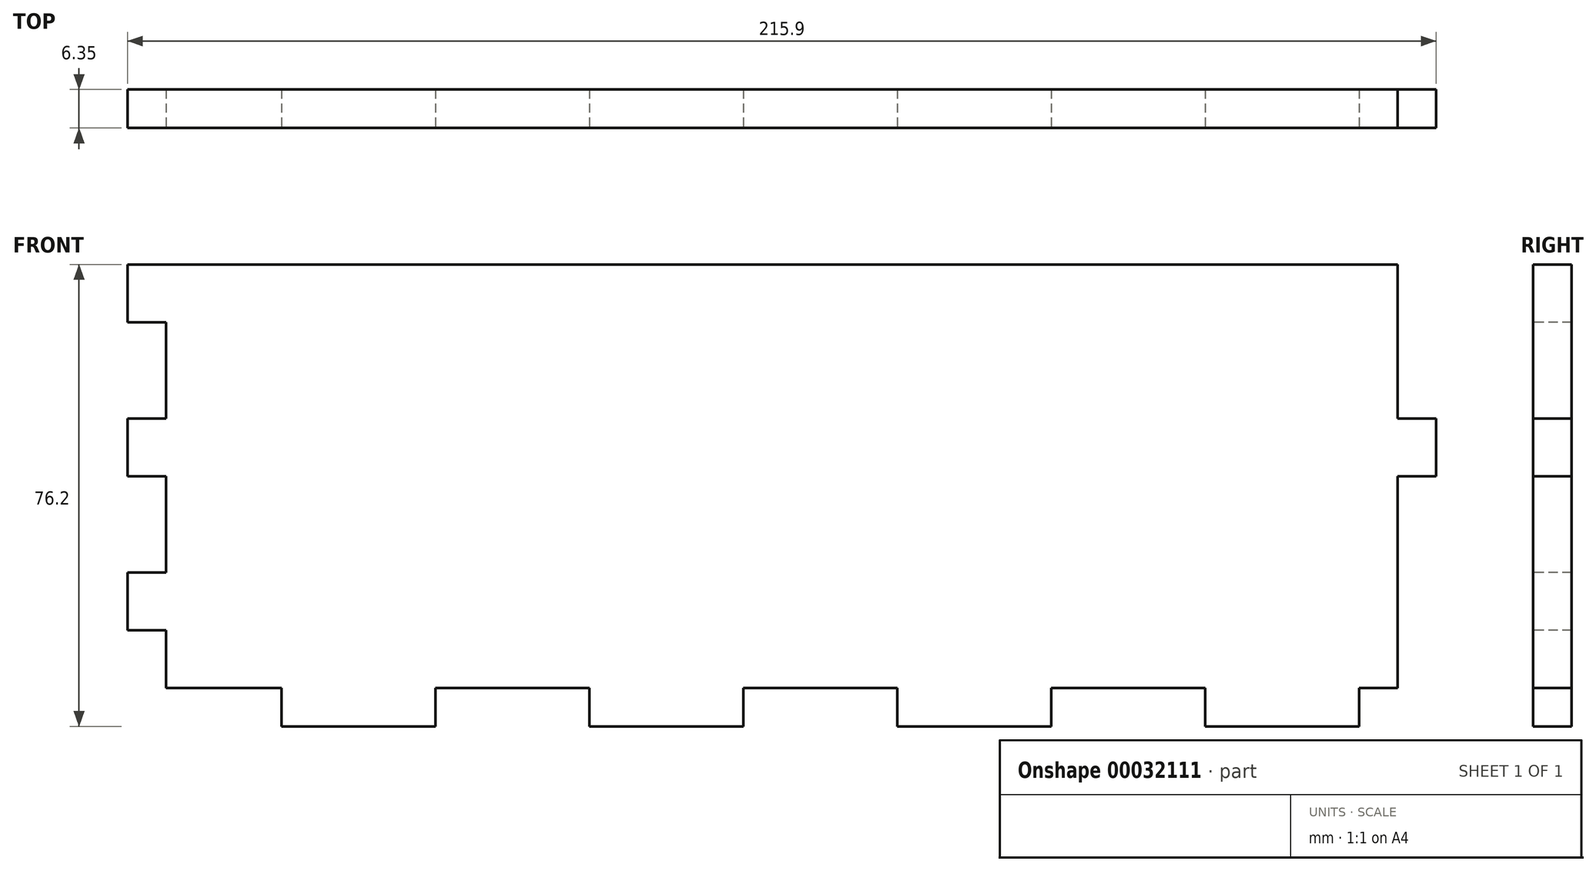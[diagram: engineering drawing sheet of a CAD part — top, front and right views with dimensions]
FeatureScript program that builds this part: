
annotation { "Feature Type Name" : "Feature", "Feature Type Description" : "" }
export const myFeature = defineFeature(function(context is Context, id is Id, definition is map)
    precondition{}
    {
        {
            var Q0;
            Q0=qCreatedBy(makeId("Front.planeOp"),FACE);
            var sketch = newSketch(context, id + "F0", { "sketchPlane" : qUnion([Q0])});
            skLineSegment(sketch, "E0.bottom", {"start": v(0, 0) * mm, "end": v(215.9, 0) * mm});
            skLineSegment(sketch, "E0.top", {"start": v(0, 76.2) * mm, "end": v(215.9, 76.2) * mm});
            skLineSegment(sketch, "E0.left", {"start": v(0, 0) * mm, "end": v(0, 76.2) * mm});
            skLineSegment(sketch, "E0.right", {"start": v(215.9, 0) * mm, "end": v(215.9, 76.2) * mm});
            skSolve(sketch);
        }
        {
            var Q0;
            Q0=makeQuery(id+"F0.imprint","IMPRINT",FACE,{"disambiguationData":[TD([[makeQuery(id+"F0.imprint","IMPRINT",EDGE,{"derivedFrom":sQuery(id+"F0.wireOp",EDGE,"E0.bottom")}),1.0]])]});
            extrude(context, id + "F1", {"entities" : qUnion([Q0]), "depth" : 6.35 * mm});
        }
        {
            var Q0;
            Q0=makeQuery(id+"F1.opExtrude","CAP_FACE",FACE,{"disambiguationData":[OSD([sQuery(id+"F0.wireOp",EDGE,"E0.bottom"),sQuery(id+"F0.wireOp",EDGE,"E0.top"),sQuery(id+"F0.wireOp",EDGE,"E0.left"),sQuery(id+"F0.wireOp",EDGE,"E0.right")])],"isStart":false});
            var sketch = newSketch(context, id + "F2", { "sketchPlane" : qUnion([Q0])});
            skLineSegment(sketch, "E1.bottom", {"start": v(0, 66.68) * mm, "end": v(6.35, 66.68) * mm});
            skLineSegment(sketch, "E1.top", {"start": v(0, 50.8) * mm, "end": v(6.35, 50.8) * mm});
            skLineSegment(sketch, "E1.left", {"start": v(0, 66.68) * mm, "end": v(0, 50.8) * mm});
            skLineSegment(sketch, "E1.right", {"start": v(6.35, 66.68) * mm, "end": v(6.35, 50.8) * mm});
            skLineSegment(sketch, "E2.bottom", {"start": v(0, 41.28) * mm, "end": v(6.35, 41.28) * mm});
            skLineSegment(sketch, "E2.top", {"start": v(0, 25.4) * mm, "end": v(6.35, 25.4) * mm});
            skLineSegment(sketch, "E2.left", {"start": v(0, 41.28) * mm, "end": v(0, 25.4) * mm});
            skLineSegment(sketch, "E2.right", {"start": v(6.35, 41.28) * mm, "end": v(6.35, 25.4) * mm});
            skLineSegment(sketch, "E3.bottom", {"start": v(0, 15.88) * mm, "end": v(6.35, 15.88) * mm});
            skLineSegment(sketch, "E3.top", {"start": v(0, 6.35) * mm, "end": v(6.35, 6.35) * mm});
            skLineSegment(sketch, "E3.left", {"start": v(0, 15.88) * mm, "end": v(0, 6.35) * mm});
            skLineSegment(sketch, "E3.right", {"start": v(6.35, 15.88) * mm, "end": v(6.35, 6.35) * mm});
            skLineSegment(sketch, "E4", {"start": v(107.95, 76.2) * mm, "end": v(107.95, 0) * mm, "construction": true});
            skLineSegment(sketch, "E5.MirrorCS", {"start": v(209.55, 15.88) * mm, "end": v(209.55, 6.35) * mm});
            skLineSegment(sketch, "E6.MirrorCS", {"start": v(215.9, 15.88) * mm, "end": v(215.9, 6.35) * mm});
            skLineSegment(sketch, "E7.MirrorCS", {"start": v(215.9, 6.35) * mm, "end": v(209.55, 6.35) * mm});
            skLineSegment(sketch, "E8.MirrorCS", {"start": v(215.9, 15.88) * mm, "end": v(209.55, 15.88) * mm});
            skLineSegment(sketch, "E9.MirrorCS", {"start": v(215.9, 41.28) * mm, "end": v(209.55, 41.28) * mm});
            skLineSegment(sketch, "E10.MirrorCS", {"start": v(215.9, 25.4) * mm, "end": v(209.55, 25.4) * mm});
            skLineSegment(sketch, "E11.MirrorCS", {"start": v(215.9, 66.68) * mm, "end": v(209.55, 66.68) * mm});
            skLineSegment(sketch, "E12.MirrorCS", {"start": v(215.9, 50.8) * mm, "end": v(209.55, 50.8) * mm});
            skLineSegment(sketch, "E13.MirrorCS", {"start": v(209.55, 41.28) * mm, "end": v(209.55, 25.4) * mm});
            skLineSegment(sketch, "E14.MirrorCS", {"start": v(215.9, 41.28) * mm, "end": v(215.9, 25.4) * mm});
            skLineSegment(sketch, "E15.MirrorCS", {"start": v(209.55, 66.68) * mm, "end": v(209.55, 50.8) * mm});
            skLineSegment(sketch, "E16.MirrorCS", {"start": v(215.9, 66.68) * mm, "end": v(215.9, 50.8) * mm});
            skSolve(sketch);
        }
        {
            var Q0;
            Q0 = qSketchRegion(id + "F2", true);
            extrude(context, id + "F3", {"entities" : qUnion([Q0]), "operationType" : NewBodyOperationType.REMOVE, "endBound" : BoundingType.UP_TO_NEXT, "oppositeDirection" : true, "depth" : 25.4 * mm});
        }
        {
            var Q0;
            Q0=makeQuery(id+"F1.opExtrude","CAP_FACE",FACE,{"disambiguationData":[OSD([sQuery(id+"F0.wireOp",EDGE,"E0.bottom"),sQuery(id+"F0.wireOp",EDGE,"E0.top"),sQuery(id+"F0.wireOp",EDGE,"E0.left"),sQuery(id+"F0.wireOp",EDGE,"E0.right")])],"isStart":false});
            var sketch = newSketch(context, id + "F4", { "sketchPlane" : qUnion([Q0])});
            skLineSegment(sketch, "E17.bottom", {"start": v(0, 0) * mm, "end": v(25.4, 0) * mm});
            skLineSegment(sketch, "E17.top", {"start": v(0, 6.35) * mm, "end": v(25.4, 6.35) * mm});
            skLineSegment(sketch, "E17.left", {"start": v(0, 0) * mm, "end": v(0, 6.35) * mm});
            skLineSegment(sketch, "E17.right", {"start": v(25.4, 0) * mm, "end": v(25.4, 6.35) * mm});
            skLineSegment(sketch, "E18.1.0.0", {"start": v(76.2, 0) * mm, "end": v(76.2, 6.35) * mm});
            skLineSegment(sketch, "E18.1.0.1", {"start": v(50.8, 0) * mm, "end": v(50.8, 6.35) * mm});
            skLineSegment(sketch, "E18.1.0.2", {"start": v(50.8, 6.35) * mm, "end": v(76.2, 6.35) * mm});
            skLineSegment(sketch, "E18.1.0.3", {"start": v(50.8, 0) * mm, "end": v(76.2, 0) * mm});
            skLineSegment(sketch, "E18.2.0.0", {"start": v(127, 0) * mm, "end": v(127, 6.35) * mm});
            skLineSegment(sketch, "E18.2.0.1", {"start": v(101.6, 0) * mm, "end": v(101.6, 6.35) * mm});
            skLineSegment(sketch, "E18.2.0.2", {"start": v(101.6, 6.35) * mm, "end": v(127, 6.35) * mm});
            skLineSegment(sketch, "E18.2.0.3", {"start": v(101.6, 0) * mm, "end": v(127, 0) * mm});
            skLineSegment(sketch, "E18.3.0.0", {"start": v(177.8, 0) * mm, "end": v(177.8, 6.35) * mm});
            skLineSegment(sketch, "E18.3.0.1", {"start": v(152.4, 0) * mm, "end": v(152.4, 6.35) * mm});
            skLineSegment(sketch, "E18.3.0.2", {"start": v(152.4, 6.35) * mm, "end": v(177.8, 6.35) * mm});
            skLineSegment(sketch, "E18.3.0.3", {"start": v(152.4, 0) * mm, "end": v(177.8, 0) * mm});
            skLineSegment(sketch, "E18.4.0.0", {"start": v(228.6, 0) * mm, "end": v(228.6, 6.35) * mm});
            skLineSegment(sketch, "E18.4.0.1", {"start": v(203.2, 0) * mm, "end": v(203.2, 6.35) * mm});
            skLineSegment(sketch, "E18.4.0.2", {"start": v(203.2, 6.35) * mm, "end": v(228.6, 6.35) * mm});
            skLineSegment(sketch, "E18.4.0.3", {"start": v(203.2, 0) * mm, "end": v(228.6, 0) * mm});
            skLineSegment(sketch, "E18.direction1", {"start": v(25.4, 0) * mm, "end": v(76.2, 0) * mm, "construction": true});
            skSolve(sketch);
        }
        {
            var Q0;
            Q0 = qSketchRegion(id + "F4", true);
            extrude(context, id + "F5", {"entities" : qUnion([Q0]), "operationType" : NewBodyOperationType.REMOVE, "endBound" : BoundingType.THROUGH_ALL, "oppositeDirection" : true, "depth" : 25.4 * mm});
        }
        {
            var Q0;
            Q0=makeQuery(id+"F1.opExtrude","CAP_FACE",FACE,{"disambiguationData":[OSD([sQuery(id+"F0.wireOp",EDGE,"E0.bottom"),sQuery(id+"F0.wireOp",EDGE,"E0.top"),sQuery(id+"F0.wireOp",EDGE,"E0.left"),sQuery(id+"F0.wireOp",EDGE,"E0.right")])],"isStart":false});
            var sketch = newSketch(context, id + "F6", { "sketchPlane" : qUnion([Q0])});
            skLineSegment(sketch, "E19.bottom", {"start": v(209.55, 15.88) * mm, "end": v(215.9, 15.88) * mm});
            skLineSegment(sketch, "E19.top", {"start": v(209.55, 25.4) * mm, "end": v(215.9, 25.4) * mm});
            skLineSegment(sketch, "E19.left", {"start": v(209.55, 15.88) * mm, "end": v(209.55, 25.4) * mm});
            skLineSegment(sketch, "E19.right", {"start": v(215.9, 15.88) * mm, "end": v(215.9, 25.4) * mm});
            skLineSegment(sketch, "E20.bottom", {"start": v(209.55, 66.68) * mm, "end": v(215.9, 66.68) * mm});
            skLineSegment(sketch, "E20.top", {"start": v(209.55, 76.2) * mm, "end": v(215.9, 76.2) * mm});
            skLineSegment(sketch, "E20.left", {"start": v(209.55, 66.68) * mm, "end": v(209.55, 76.2) * mm});
            skLineSegment(sketch, "E20.right", {"start": v(215.9, 66.68) * mm, "end": v(215.9, 76.2) * mm});
            skSolve(sketch);
        }
        {
            var Q0;
            Q0 = qSketchRegion(id + "F6", true);
            extrude(context, id + "F7", {"entities" : qUnion([Q0]), "operationType" : NewBodyOperationType.REMOVE, "endBound" : BoundingType.UP_TO_NEXT, "oppositeDirection" : true, "depth" : 25.4 * mm});
        }
    });
